# Revit family: Plate_System_Water_Coolers-Zurn-Z1251
name_source: partatom
category: Plumbing Fixtures
units: mm (PartAtom-declared; Revit-internal decimal feet)

## family parameters
Cut with Voids When Loaded = No
Host = Face
Maintain Annotation Orientation = No
OmniClass Number = 23.65.70.14.11
OmniClass Title = Drinking Fountains/Coolers
Part Type = Normal
Room Calculation Point = No
Round Connector Dimension = Use Radius
Shared = No

## types (4) — shared parameters
CW Connection = No
D Dimension = 4 "
Default Elevation = 25 "
Description = CONCEALED ARM SYSTEM WALL SUPPORTED
E Dimension = 7 "
Enter_Hanger Adjustment = 2.125 "
Enter_Hanger Horizontal Adjustment = 1.75 "
F Dimension = 7 "
G Dimension = 18.5 "
HW Connection = No
Hanger Dimension = 2.125 "
Hanger Horizontal Dimension = 1.75 "
Main Material = Iron - Zurn - Cast - Painted - Blue
Manufacturer = Zurn Water, LLC
Manufacturer Brand = Zurn
Model = Z1251
Modified Date = 10/31/2025
Product Documentation Link = https://files.zurn.com
Product Page URL = https://www.zurn.com
Product data url = https://www.bimobject.com
URL = www.zurn.com
Vent Connection = No
WFU = 1
Waste Connection = Yes
zero-valued in all types: CWFU, HWFU

## per-type parameters (varying)
| type | A Distance | Assembly Code |
| American Standard-Roxalyn (0914.043) | 16.5 " | D2030100 |
| American Standard-Roxalyn (0914.076) | 16.5 " |  |
| American Standard-Roxalyn (0914.134) | 20 " |  |
| American Standard-Surgeons (9010.018) | 24 " |  |

## geometry (parser evidence)
native form markers: Sweep x5
no freeform markers — native parametric forms only
